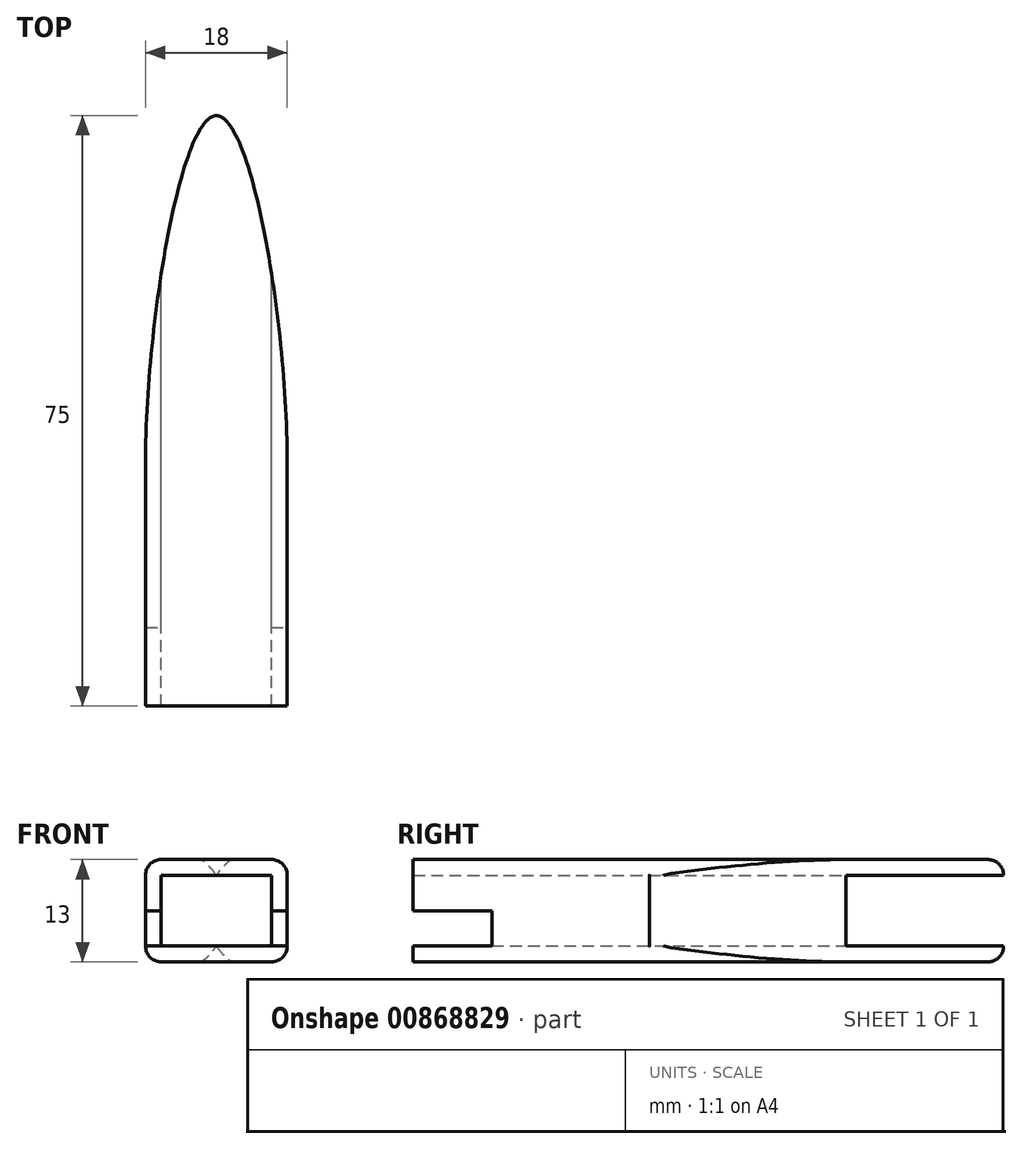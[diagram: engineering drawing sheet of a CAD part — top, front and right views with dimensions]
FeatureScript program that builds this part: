
annotation { "Feature Type Name" : "Feature", "Feature Type Description" : "" }
export const myFeature = defineFeature(function(context is Context, id is Id, definition is map)
    precondition{}
    {
        {
            var Q0;
            Q0=qCreatedBy(makeId("Front.planeOp"),FACE);
            var sketch = newSketch(context, id + "F0", { "sketchPlane" : qUnion([Q0])});
            skLineSegment(sketch, "E0.bottom", {"start": v(-9, 6.5) * mm, "end": v(9, 6.5) * mm});
            skLineSegment(sketch, "E0.top", {"start": v(-9, -6.5) * mm, "end": v(9, -6.5) * mm});
            skLineSegment(sketch, "E0.left", {"start": v(-9, 6.5) * mm, "end": v(-9, -6.5) * mm});
            skLineSegment(sketch, "E0.right", {"start": v(9, 6.5) * mm, "end": v(9, -6.5) * mm});
            skPoint(sketch, "E0.middle", {"position": v(0, 0) * mm});
            skLineSegment(sketch, "E1.bottom", {"start": v(-7, 4.5) * mm, "end": v(7, 4.5) * mm});
            skLineSegment(sketch, "E1.top", {"start": v(-7, -4.5) * mm, "end": v(7, -4.5) * mm});
            skLineSegment(sketch, "E1.left", {"start": v(-7, 4.5) * mm, "end": v(-7, -4.5) * mm});
            skLineSegment(sketch, "E1.right", {"start": v(7, 4.5) * mm, "end": v(7, -4.5) * mm});
            skSolve(sketch);
        }
        {
            var Q0;
            Q0=makeQuery(id+"F0.imprint","IMPRINT",FACE,{"disambiguationData":[TD([[makeQuery(id+"F0.imprint","IMPRINT",EDGE,{"derivedFrom":sQuery(id+"F0.wireOp",EDGE,"E0.bottom")}),-1.0]])]});
            extrude(context, id + "F1", {"entities" : qUnion([Q0]), "depth" : 75 * mm, "offsetDistance" : 25 * mm});
        }
        {
            var Q0;
            Q0=makeQuery(id+"F1.opExtrude","SWEPT_EDGE",EDGE,{"disambiguationData":[OSD([sQuery(id+"F0.wireOp",EDGE,"E0.bottom"),sQuery(id+"F0.wireOp",EDGE,"E0.left")])]});
            var Q1;
            Q1=makeQuery(id+"F1.opExtrude","SWEPT_EDGE",EDGE,{"disambiguationData":[OSD([sQuery(id+"F0.wireOp",EDGE,"E0.bottom"),sQuery(id+"F0.wireOp",EDGE,"E0.right")])]});
            var Q2;
            Q2=makeQuery(id+"F1.opExtrude","CAP_EDGE",EDGE,{"disambiguationData":[OSD([sQuery(id+"F0.wireOp",EDGE,"E0.right")])],"isStart":true});
            var Q3;
            Q3=makeQuery(id+"F1.opExtrude","CAP_EDGE",EDGE,{"disambiguationData":[OSD([sQuery(id+"F0.wireOp",EDGE,"E0.bottom")])],"isStart":true});
            var Q4;
            Q4=makeQuery(id+"F1.opExtrude","CAP_EDGE",EDGE,{"disambiguationData":[OSD([sQuery(id+"F0.wireOp",EDGE,"E0.left")])],"isStart":true});
            var Q5;
            Q5=makeQuery(id+"F1.opExtrude","CAP_EDGE",EDGE,{"disambiguationData":[OSD([sQuery(id+"F0.wireOp",EDGE,"E0.top")])],"isStart":true});
            var Q6;
            Q6=makeQuery(id+"F1.opExtrude","SWEPT_EDGE",EDGE,{"disambiguationData":[OSD([sQuery(id+"F0.wireOp",EDGE,"E0.top"),sQuery(id+"F0.wireOp",EDGE,"E0.left")])]});
            var Q7;
            Q7=makeQuery(id+"F1.opExtrude","SWEPT_EDGE",EDGE,{"disambiguationData":[OSD([sQuery(id+"F0.wireOp",EDGE,"E0.top"),sQuery(id+"F0.wireOp",EDGE,"E0.right")])]});
            fillet(context, id + "F2", {"entities" : qUnion([Q0, Q1, Q2, Q3, Q4, Q5, Q6, Q7]), "radius" : 2 * mm, "tangentPropagation" : true, "allowEdgeOverflow" : false});
        }
        {
            var Q0;
            Q0=makeQuery(id+"F1.opExtrude","SWEPT_FACE",FACE,{"disambiguationData":[OSD([sQuery(id+"F0.wireOp",EDGE,"E0.bottom")])]});
            var sketch = newSketch(context, id + "F3", { "sketchPlane" : qUnion([Q0])});
            skFitSpline(sketch, "E2", {"points": [v(9, -45) * mm, v(0, 0) * mm, v(-9, -45) * mm], "startDerivative": vector(0.95, 106.9) * mm, "endDerivative": vector(0.77, -107.46) * mm});
            skLineSegment(sketch, "E3", {"start": v(-9.67, -45) * mm, "end": v(15.16, -45) * mm, "construction": true});
            skLineSegment(sketch, "E4", {"start": v(-9, -45) * mm, "end": v(-14.55, 3.23) * mm});
            skLineSegment(sketch, "E5", {"start": v(-14.55, 3.23) * mm, "end": v(17.24, 3.23) * mm});
            skLineSegment(sketch, "E6", {"start": v(17.24, 3.23) * mm, "end": v(9, -45) * mm});
            skSolve(sketch);
        }
        {
            var Q0;
            {var subQ0=sQuery(id+"F3.wireOp",EDGE,"E4");Q0=makeQuery(id+"F3.imprint","IMPRINT",FACE,{"disambiguationData":[TD([[makeQuery(id+"F3.imprint","IMPRINT",EDGE,{"derivedFrom":subQ0}),-1.0]])]});}
            var Q1;
            {var subQ0=sQuery(id+"F3.wireOp",EDGE,"E2");var subQ1=sQuery(id+"F0.wireOp",EDGE,"E0.bottom");var subQ2=makeQuery(id+"F1.opExtrude","SWEPT_FACE",FACE,{"disambiguationData":[OSD([subQ1])]});var subQ5=makeQuery(id+"F2.opFillet","BLEND_EDGE",EDGE,{"blendedFrom":[makeQuery(id+"F1.opExtrude","CAP_EDGE",EDGE,{"disambiguationData":[OSD([subQ1])],"isStart":true}),subQ2],"blendedInto":[subQ2]});var subQ6=makeQuery(id+"F3.imprint","INTERSECT",VERTEX,{"disambiguationData":[OD(1.0)],"derivedFrom":[subQ5,subQ0]});Q1=makeQuery(id+"F3.imprint","IMPRINT",FACE,{"disambiguationData":[TD([[makeQuery(id+"F3.imprint","IMPRINT",EDGE,{"disambiguationData":[TD([[subQ6,-1.0]])],"derivedFrom":subQ0}),-1.0]])]});}
            var Q2;
            {var subQ0=sQuery(id+"F3.wireOp",EDGE,"E2");var subQ1=sQuery(id+"F0.wireOp",EDGE,"E0.bottom");var subQ2=makeQuery(id+"F1.opExtrude","SWEPT_FACE",FACE,{"disambiguationData":[OSD([subQ1])]});var subQ5=makeQuery(id+"F2.opFillet","BLEND_EDGE",EDGE,{"blendedFrom":[makeQuery(id+"F1.opExtrude","CAP_EDGE",EDGE,{"disambiguationData":[OSD([subQ1])],"isStart":true}),subQ2],"blendedInto":[subQ2]});var subQ6=makeQuery(id+"F3.imprint","INTERSECT",VERTEX,{"disambiguationData":[OD(0.0)],"derivedFrom":[subQ5,subQ0]});Q2=makeQuery(id+"F3.imprint","IMPRINT",FACE,{"disambiguationData":[TD([[makeQuery(id+"F3.imprint","IMPRINT",EDGE,{"disambiguationData":[TD([[subQ6,1.0]])],"derivedFrom":subQ0}),-1.0]])]});}
            extrude(context, id + "F4", {"entities" : qUnion([Q0, Q1, Q2]), "operationType" : NewBodyOperationType.REMOVE, "oppositeDirection" : true, "depth" : 25 * mm, "offsetDistance" : 25 * mm});
        }
        {
            var Q0;
            {var subQ0=sQuery(id+"F0.wireOp",EDGE,"E0.right");Q0=makeQuery(id+"F4.boolean.opBoolean","SPLIT",FACE,{"disambiguationData":[TD([makeQuery(id+"F4.opExtrude","SWEPT_FACE",FACE,{"disambiguationData":[OSD([sQuery(id+"F3.wireOp",EDGE,"E6")])]})])],"derivedFrom":makeQuery(id+"F1.opExtrude","SWEPT_FACE",FACE,{"disambiguationData":[OSD([subQ0])]})});}
            var sketch = newSketch(context, id + "F5", { "sketchPlane" : qUnion([Q0])});
            skLineSegment(sketch, "E7.bottom", {"start": v(-75, 0) * mm, "end": v(-65, 0) * mm});
            skLineSegment(sketch, "E7.top", {"start": v(-75, -4.5) * mm, "end": v(-65, -4.5) * mm});
            skLineSegment(sketch, "E7.left", {"start": v(-75, 0) * mm, "end": v(-75, -4.5) * mm});
            skLineSegment(sketch, "E7.right", {"start": v(-65, 0) * mm, "end": v(-65, -4.5) * mm});
            skSolve(sketch);
        }
        {
            var Q0;
            Q0=makeQuery(id+"F5.imprint","IMPRINT",FACE,{"disambiguationData":[TD([[makeQuery(id+"F5.imprint","IMPRINT",EDGE,{"derivedFrom":sQuery(id+"F5.wireOp",EDGE,"E7.bottom")}),-1.0]])]});
            extrude(context, id + "F6", {"entities" : qUnion([Q0]), "operationType" : NewBodyOperationType.REMOVE, "oppositeDirection" : true, "depth" : 25 * mm, "offsetDistance" : 25 * mm});
        }
    });
